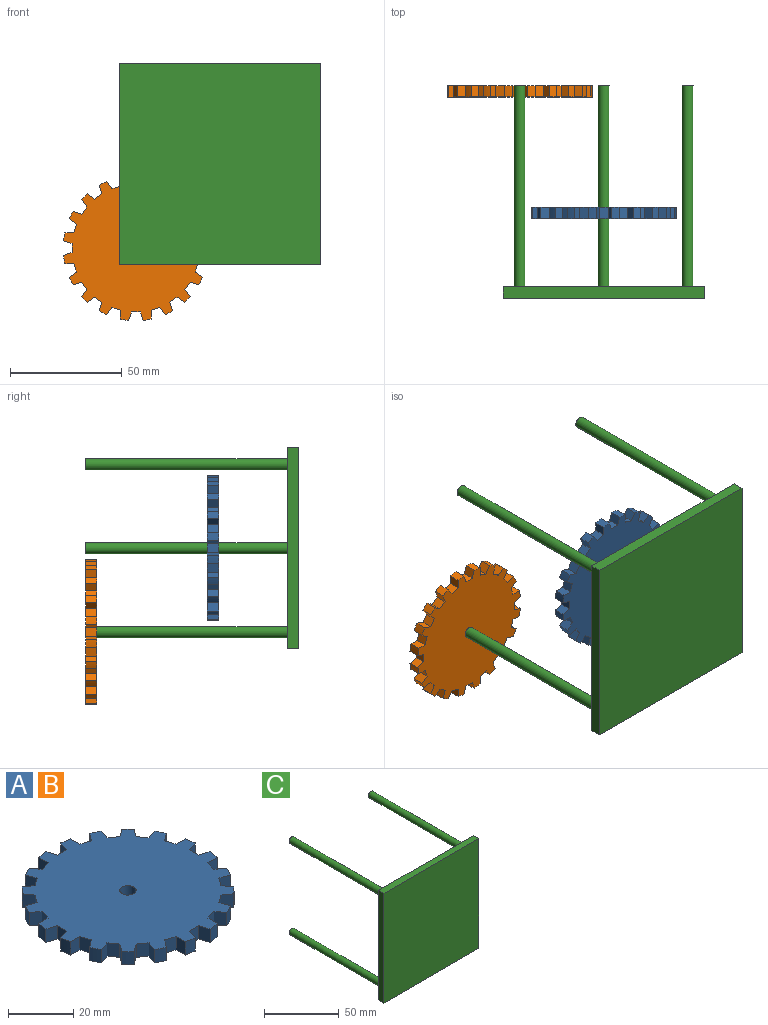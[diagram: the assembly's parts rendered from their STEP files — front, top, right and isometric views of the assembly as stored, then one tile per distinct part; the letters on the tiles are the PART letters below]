
ASSEMBLY  parts=3 mates=2
PART A: 83 faces, bbox 64.7x64.7x5 mm
  f0: cylinder r=32.5mm len=5mm, axis (0,0,-1), area 18.6mm2, adj f19,f21,f77,f82
  f1: cylinder r=32.5mm len=5mm, axis (0,0,-1), area 18.6mm2, adj f19,f21,f74,f79
  f2: cylinder r=32.5mm len=5mm, axis (0,0,-1), area 18.6mm2, adj f19,f21,f71,f76
  f3: cylinder r=32.5mm len=5mm, axis (0,0,-1), area 18.6mm2, adj f19,f21,f68,f73
  f4: cylinder r=32.5mm len=5mm, axis (0,0,-1), area 18.6mm2, adj f19,f21,f65,f70
  f5: cylinder r=32.5mm len=5mm, axis (0,0,-1), area 18.6mm2, adj f19,f21,f62,f67
  f6: cylinder r=32.5mm len=5mm, axis (0,0,-1), area 18.6mm2, adj f19,f21,f59,f64
  f7: cylinder r=32.5mm len=5mm, axis (0,0,-1), area 18.6mm2, adj f19,f21,f56,f61
  f8: cylinder r=32.5mm len=5mm, axis (0,0,-1), area 18.6mm2, adj f19,f21,f55,f58
  f9: cylinder r=32.5mm len=5mm, axis (0,0,-1), area 18.6mm2, adj f19,f21,f50,f54
  f10: cylinder r=32.5mm len=5mm, axis (0,0,-1), area 18.6mm2, adj f19,f21,f47,f52
  f11: cylinder r=32.5mm len=5mm, axis (0,0,-1), area 18.6mm2, adj f19,f21,f44,f49
  f12: cylinder r=32.5mm len=5mm, axis (0,0,-1), area 18.6mm2, adj f19,f21,f41,f46
  f13: cylinder r=32.5mm len=5mm, axis (0,0,-1), area 18.6mm2, adj f19,f21,f38,f43
  f14: cylinder r=32.5mm len=5mm, axis (0,0,-1), area 18.6mm2, adj f19,f21,f35,f40
  f15: cylinder r=32.5mm len=5mm, axis (0,0,-1), area 18.6mm2, adj f19,f21,f32,f37
  f16: cylinder r=32.5mm len=5mm, axis (0,0,-1), area 18.6mm2, adj f19,f21,f29,f34
  f17: cylinder r=32.5mm len=5mm, axis (0,0,-1), area 18.6mm2, adj f19,f21,f26,f31
  f18: cylinder r=32.5mm len=5mm, axis (0,0,-1), area 18.6mm2, adj f19,f21,f23,f28
  f19: plane 64.68x64.68mm, normal (0,0,1), area 2886.3mm2, adj f0,f1,f2,f3,f4,f5,f6,f7
  f20: cylinder r=32.5mm len=5mm, axis (0,0,-1), area 18.6mm2, adj f19,f21,f25,f80
  f21: plane 64.68x64.68mm, normal (0,0,-1), area 2886.3mm2, adj f0,f1,f2,f3,f4,f5,f6,f7
  f22: cylinder r=2.5mm len=5mm, axis (0,0,1), area 78.5mm2, adj f19,f21
  f23: plane 5x4mm, normal (0,1,0), area 20mm2, adj f18,f19,f21,f24
  f24: plane 5x3.8mm, normal (-0.95,0.31,0), area 20mm2, adj f19,f21,f23,f25
  f25: plane 5x3.24mm, normal (-0.59,-0.81,0), area 20mm2, adj f19,f20,f21,f24
  f26: plane 5x3.8mm, normal (-0.31,0.95,0), area 20mm2, adj f17,f19,f21,f27
  f27: plane 5x4mm, normal (-1,0,0), area 20mm2, adj f19,f21,f26,f28
  f28: plane 5x3.8mm, normal (-0.31,-0.95,0), area 20mm2, adj f18,f19,f21,f27
  f29: plane 5x3.24mm, normal (-0.59,0.81,0), area 20mm2, adj f16,f19,f21,f30
  f30: plane 5x3.8mm, normal (-0.95,-0.31,0), area 20mm2, adj f19,f21,f29,f31
  f31: plane 5x4mm, normal (0,-1,0), area 20mm2, adj f17,f19,f21,f30
  f32: plane 5x3.24mm, normal (-0.81,0.59,0), area 20mm2, adj f15,f19,f21,f33
  f33: plane 5x3.24mm, normal (-0.81,-0.59,0), area 20mm2, adj f19,f21,f32,f34
  f34: plane 5x3.8mm, normal (0.31,-0.95,0), area 20mm2, adj f16,f19,f21,f33
  f35: plane 5x3.8mm, normal (-0.95,0.31,0), area 20mm2, adj f14,f19,f21,f36
  f36: plane 5x3.24mm, normal (-0.59,-0.81,0), area 20mm2, adj f19,f21,f35,f37
  f37: plane 5x3.24mm, normal (0.59,-0.81,0), area 20mm2, adj f15,f19,f21,f36
  f38: plane 5x4mm, normal (-1,0,0), area 20mm2, adj f13,f19,f21,f39
  f39: plane 5x3.8mm, normal (-0.31,-0.95,0), area 20mm2, adj f19,f21,f38,f40
  f40: plane 5x3.24mm, normal (0.81,-0.59,0), area 20mm2, adj f14,f19,f21,f39
  f41: plane 5x3.8mm, normal (-0.95,-0.31,0), area 20mm2, adj f12,f19,f21,f42
  f42: plane 5x4mm, normal (0,-1,0), area 20mm2, adj f19,f21,f41,f43
  f43: plane 5x3.8mm, normal (0.95,-0.31,0), area 20mm2, adj f13,f19,f21,f42
  f44: plane 5x3.24mm, normal (-0.81,-0.59,0), area 20mm2, adj f11,f19,f21,f45
  f45: plane 5x3.8mm, normal (0.31,-0.95,0), area 20mm2, adj f19,f21,f44,f46
  f46: plane 5x4mm, normal (1,0,0), area 20mm2, adj f12,f19,f21,f45
  f47: plane 5x3.24mm, normal (-0.59,-0.81,0), area 20mm2, adj f10,f19,f21,f48
  f48: plane 5x3.24mm, normal (0.59,-0.81,0), area 20mm2, adj f19,f21,f47,f49
  f49: plane 5x3.8mm, normal (0.95,0.31,0), area 20mm2, adj f11,f19,f21,f48
  f50: plane 5x3.8mm, normal (-0.31,-0.95,0), area 20mm2, adj f9,f19,f21,f51
  f51: plane 5x3.24mm, normal (0.81,-0.59,0), area 20mm2, adj f19,f21,f50,f52
  f52: plane 5x3.24mm, normal (0.81,0.59,0), area 20mm2, adj f10,f19,f21,f51
  f53: plane 5x3.8mm, normal (0.95,-0.31,0), area 20mm2, adj f19,f21,f54,f55
  f54: plane 5x3.24mm, normal (0.59,0.81,0), area 20mm2, adj f9,f19,f21,f53
  f55: plane 5x4mm, normal (0,-1,0), area 20mm2, adj f8,f19,f21,f53
  f56: plane 5x3.8mm, normal (0.31,-0.95,0), area 20mm2, adj f7,f19,f21,f57
  f57: plane 5x4mm, normal (1,0,0), area 20mm2, adj f19,f21,f56,f58
  f58: plane 5x3.8mm, normal (0.31,0.95,0), area 20mm2, adj f8,f19,f21,f57
  f59: plane 5x3.24mm, normal (0.59,-0.81,0), area 20mm2, adj f6,f19,f21,f60
  f60: plane 5x3.8mm, normal (0.95,0.31,0), area 20mm2, adj f19,f21,f59,f61
  f61: plane 5x4mm, normal (0,1,0), area 20mm2, adj f7,f19,f21,f60
  f62: plane 5x3.24mm, normal (0.81,-0.59,0), area 20mm2, adj f5,f19,f21,f63
  f63: plane 5x3.24mm, normal (0.81,0.59,0), area 20mm2, adj f19,f21,f62,f64
  f64: plane 5x3.8mm, normal (-0.31,0.95,0), area 20mm2, adj f6,f19,f21,f63
  f65: plane 5x3.8mm, normal (0.95,-0.31,0), area 20mm2, adj f4,f19,f21,f66
  f66: plane 5x3.24mm, normal (0.59,0.81,0), area 20mm2, adj f19,f21,f65,f67
  f67: plane 5x3.24mm, normal (-0.59,0.81,0), area 20mm2, adj f5,f19,f21,f66
  f68: plane 5x4mm, normal (1,0,0), area 20mm2, adj f3,f19,f21,f69
  f69: plane 5x3.8mm, normal (0.31,0.95,0), area 20mm2, adj f19,f21,f68,f70
  f70: plane 5x3.24mm, normal (-0.81,0.59,0), area 20mm2, adj f4,f19,f21,f69
  f71: plane 5x3.8mm, normal (0.95,0.31,0), area 20mm2, adj f2,f19,f21,f72
  f72: plane 5x4mm, normal (0,1,0), area 20mm2, adj f19,f21,f71,f73
  f73: plane 5x3.8mm, normal (-0.95,0.31,0), area 20mm2, adj f3,f19,f21,f72
  f74: plane 5x3.24mm, normal (0.81,0.59,0), area 20mm2, adj f1,f19,f21,f75
  f75: plane 5x3.8mm, normal (-0.31,0.95,0), area 20mm2, adj f19,f21,f74,f76
  f76: plane 5x4mm, normal (-1,0,0), area 20mm2, adj f2,f19,f21,f75
  f77: plane 5x3.24mm, normal (0.59,0.81,0), area 20mm2, adj f0,f19,f21,f78
  f78: plane 5x3.24mm, normal (-0.59,0.81,0), area 20mm2, adj f19,f21,f77,f79
  f79: plane 5x3.8mm, normal (-0.95,-0.31,0), area 20mm2, adj f1,f19,f21,f78
  f80: plane 5x3.8mm, normal (0.31,0.95,0), area 20mm2, adj f19,f20,f21,f81
  f81: plane 5x3.24mm, normal (-0.81,0.59,0), area 20mm2, adj f19,f21,f80,f82
  f82: plane 5x3.24mm, normal (-0.81,-0.59,0), area 20mm2, adj f0,f19,f21,f81
PART B: same geometry as A
PART C: 16 faces, bbox 90x95x90 mm
  f0: plane 90x5mm, normal (0,0,-1), area 450mm2, adj f1,f3,f4,f5
  f1: plane 90x5mm, normal (1,0,0), area 450mm2, adj f0,f2,f4,f5
  f2: plane 90x5mm, normal (0,0,1), area 450mm2, adj f1,f3,f4,f5
  f3: plane 90x5mm, normal (-1,0,0), area 450mm2, adj f0,f2,f4,f5
  f4: plane 90x90mm, normal (0,-1,0), area 8100mm2, adj f0,f1,f2,f3
  f5: plane 90x90mm, normal (0,1,0), area 8001.8mm2, adj f0,f1,f2,f3,f6,f8,f10,f12
  f6: cylinder r=2.5mm len=90mm, axis (0,-1,0), area 1413.7mm2, adj f5,f7
  f7: plane 5x5mm, normal (0,1,0), area 19.6mm2, adj f6
  f8: cylinder r=2.5mm len=90mm, axis (0,-1,0), area 1413.7mm2, adj f5,f9
  f9: plane 5x5mm, normal (0,1,0), area 19.6mm2, adj f8
  f10: cylinder r=2.5mm len=90mm, axis (0,-1,0), area 1413.7mm2, adj f5,f11
  f11: plane 5x5mm, normal (0,1,0), area 19.6mm2, adj f10
  f12: cylinder r=2.5mm len=90mm, axis (0,-1,0), area 1413.7mm2, adj f5,f13
  f13: plane 5x5mm, normal (0,1,0), area 19.6mm2, adj f12
  f14: cylinder r=2.5mm len=90mm, axis (0,-1,0), area 1413.7mm2, adj f5,f15
  f15: plane 5x5mm, normal (0,1,0), area 19.6mm2, adj f14
PLACE A rot(axis=(-1,0,0),90deg) t=(-19.03,37.36,12.44)mm
PLACE B rot(axis=(1,0,0),90deg) t=(-56.53,96.72,-25.06)mm
PLACE C t=(-19.03,6.72,12.44)mm
MATE revolute B.f0 <-> C.f12  axis (0,1,0) through (-56.53,96.72,-25.06)mm
MATE slider A.f0 <-> C.f6  axis (0,1,0) through (-19.03,42.36,12.44)mm
